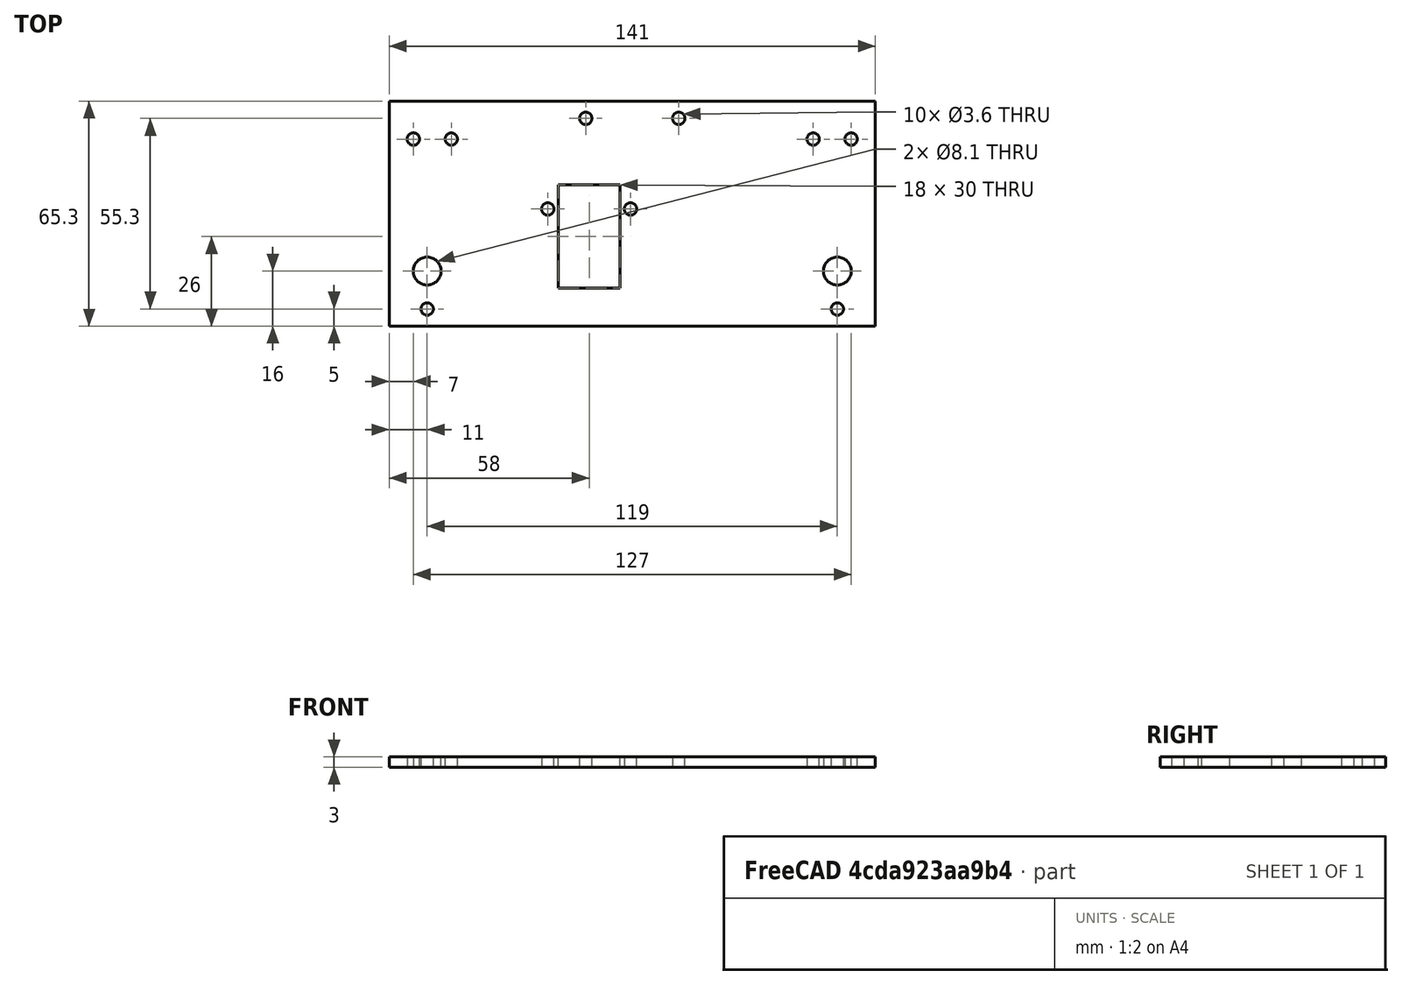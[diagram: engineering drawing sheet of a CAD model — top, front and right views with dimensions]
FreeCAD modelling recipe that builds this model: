
FCSTD DOCUMENT  (FreeCAD 0.16R6706 (Git))
Label: Plate Y Direita
License: All rights reserved
LicenseURL: http://en.wikipedia.org/wiki/All_rights_reserved
objects: Path::FeaturePython×16, Sketcher::SketchObject×1, PartDesign::Pad×1, Path::FeatureCompoundPython×1
note: 3 computed .brp shape members not serialized (recipe doc carries the construction recipe); baked Part::Feature solids carry a one-line shape summary decoded from their .brp

FEATURE [Sketcher::SketchObject] Sketch
  sketch-geometry (28):
    g0: LineSegment StartX=-141 StartY=65.3 StartZ=0 EndX=0 EndY=65.3 EndZ=0
    g1: LineSegment StartX=0 StartY=65.3 StartZ=0 EndX=0 EndY=0 EndZ=0
    g2: LineSegment StartX=0 StartY=0 StartZ=0 EndX=-141 EndY=0 EndZ=0
    g3: LineSegment StartX=-141 StartY=0 StartZ=0 EndX=-141 EndY=65.3 EndZ=0
    g4: Circle CenterX=-130 CenterY=16 CenterZ=0 NormalX=0 NormalY=0 NormalZ=1 Radius=4.05
    g5: Circle CenterX=-11 CenterY=16 CenterZ=0 NormalX=0 NormalY=0 NormalZ=1 Radius=4.05
    g6: LineSegment [constr] StartX=-130 StartY=16 StartZ=0 EndX=-11 EndY=16 EndZ=0
    g7: LineSegment [constr] StartX=-134 StartY=54.3 StartZ=0 EndX=-123 EndY=54.3 EndZ=0
    g8: Circle CenterX=-134 CenterY=54.3 CenterZ=0 NormalX=0 NormalY=0 NormalZ=1 Radius=1.8
    g9: Circle CenterX=-123 CenterY=54.3 CenterZ=0 NormalX=0 NormalY=0 NormalZ=1 Radius=1.8
    g10: LineSegment [constr] StartX=-18 StartY=54.3 StartZ=0 EndX=-7 EndY=54.3 EndZ=0
    g11: Circle CenterX=-18 CenterY=54.3 CenterZ=0 NormalX=0 NormalY=0 NormalZ=1 Radius=1.8
    g12: Circle CenterX=-7 CenterY=54.3 CenterZ=0 NormalX=0 NormalY=0 NormalZ=1 Radius=1.8
    g13: LineSegment StartX=-92 StartY=41 StartZ=0 EndX=-74 EndY=41 EndZ=0
    g14: LineSegment StartX=-74 StartY=41 StartZ=0 EndX=-74 EndY=11 EndZ=0
    g15: LineSegment StartX=-74 StartY=11 StartZ=0 EndX=-92 EndY=11 EndZ=0
    g16: LineSegment StartX=-92 StartY=11 StartZ=0 EndX=-92 EndY=41 EndZ=0
    g17: LineSegment [constr] StartX=-84 StartY=60.3 StartZ=0 EndX=-57 EndY=60.3 EndZ=0
    g18: LineSegment [constr] StartX=-70.5 StartY=60.3 StartZ=0 EndX=-70.5 EndY=65.3 EndZ=0
    g19: Circle CenterX=-84 CenterY=60.3 CenterZ=0 NormalX=0 NormalY=0 NormalZ=1 Radius=1.8
    g20: Circle CenterX=-57 CenterY=60.3 CenterZ=0 NormalX=0 NormalY=0 NormalZ=1 Radius=1.8
    g21: LineSegment [constr] StartX=-95 StartY=34 StartZ=0 EndX=-71 EndY=34 EndZ=0
    g22: Circle CenterX=-95 CenterY=34 CenterZ=0 NormalX=0 NormalY=0 NormalZ=1 Radius=1.8
    g23: Circle CenterX=-71 CenterY=34 CenterZ=0 NormalX=0 NormalY=0 NormalZ=1 Radius=1.8
    g24: LineSegment [constr] StartX=-130 StartY=5 StartZ=0 EndX=-11 EndY=5 EndZ=0
    g25: LineSegment [constr] StartX=-130 StartY=16 StartZ=0 EndX=-130 EndY=5 EndZ=0
    g26: Circle CenterX=-130 CenterY=5 CenterZ=0 NormalX=0 NormalY=0 NormalZ=1 Radius=1.8
    g27: Circle CenterX=-11 CenterY=5 CenterZ=0 NormalX=0 NormalY=0 NormalZ=1 Radius=1.8
  constraints (76):
    c: Coincident(g0,g1)
    c: Coincident(g1,g2)
    c: Coincident(g2,g3)
    c: Coincident(g3,g0)
    c: Horizontal(g0)
    c: Horizontal(g2)
    c: Vertical(g1)
    c: Vertical(g3)
    c: Coincident(g1,g-1)
    c: Radius(g4) = 4.05
    c: Equal(g4,g5) = 4.3
    c: Horizontal(g6)
    c: Coincident(g4,g6)
    c: Coincident(g5,g6)
    c: DistanceX(g2,g4) = 11
    c: DistanceX(g5,g-1) = 11
    c: DistanceX(g6,g6) = 119
    c: DistanceY(g2,g4) = 16
    c: DistanceY(g4,g0) = 49.3
    c: DistanceY(g2,g0) = 65.3
    c: Horizontal(g7)
    c: DistanceX(g7,g7) = 11
    c: Radius(g8) = 1.8
    c: Equal(g8,g9) = 1.8
    c: Coincident(g7,g9)
    c: Coincident(g7,g8)
    c: Horizontal(g10)
    c: Equal(g7,g10) = 10
    c: Equal(g8,g11) = 1.8
    c: Equal(g11,g12) = 1.8
    c: Coincident(g10,g12)
    c: Coincident(g10,g11)
    c: DistanceY(g7,g0) = 11
    c: PointOnObject(g10,g7)
    c: DistanceX(g0,g7) = 7
    c: DistanceX(g10,g0) = 7
    c: Coincident(g13,g14)
    c: Coincident(g14,g15)
    c: Coincident(g15,g16)
    c: Coincident(g16,g13)
    c: Horizontal(g13)
    c: Horizontal(g15)
    c: Vertical(g14)
    c: Vertical(g16)
    c: DistanceX(g15,g15) = 18
    c: DistanceY(g16,g16) = 30
    c: Horizontal(g17)
    c: DistanceX(g17,g17) = 27
    c: Vertical(g18)
    c: DistanceY(g18,g18) = 5
    c: Equal(g8,g19) = 1.8
    c: Equal(g8,g20) = 1.8
    c: Coincident(g17,g20)
    c: Coincident(g19,g17)
    c: Symmetric(g0,g0,g18)
    c: Symmetric(g17,g17,g18)
    c: DistanceY(g4,g13) = 25
    c: Horizontal(g21)
    c: DistanceX(g21,g21) = 24
    c: Equal(g8,g22) = 1.8
    c: Equal(g8,g23) = 1.8
    c: Coincident(g23,g21)
    c: Coincident(g21,g22)
    c: DistanceX(g21,g13) = 3
    c: DistanceY(g21,g13) = 7
    c: DistanceX(g4,g13) = 38
    c: Horizontal(g24)
    c: Equal(g6,g24) = 119
    c: Vertical(g25)
    c: Coincident(g25,g4)
    c: DistanceY(g25,g25) = 11
    c: Coincident(g24,g25)
    c: Equal(g8,g26) = 1.8
    c: Equal(g8,g27) = 1.8
    c: Coincident(g24,g27)
    c: Coincident(g24,g26)
FEATURE [PartDesign::Pad] Pad
  Length = 3
  Length2 = 100
  Sketch = -> Sketch
  Type = 0
FEATURE [Path::FeaturePython] Machine  label="Machine_"  # Path/CAM operation (typed FeaturePython)
  MachineUnits = 0
  X = 0
  X_Max = 0
  X_Min = 0
  Y = 0
  Y_Max = 0
  Y_Min = 0
  Z = 0
  Z_Max = 0
  Z_Min = 0
FEATURE [Path::FeaturePython] Tool  label="Tool1"  # Path/CAM operation (typed FeaturePython)
  SpindleDir = 0
  SpindleSpeed = 0
  ToolNumber = 1
FEATURE [Path::FeaturePython] Profile  label="Berço"  # Path/CAM operation (typed FeaturePython)
  Active = true
  Base = -> Pad
  ClearanceHeight = 3
  Direction = 1
  Edge1 = -> Pad [Edge48]
  EndPoint = (0,0,0)
  ExtendAtEnd = 0
  ExtendAtStart = 0
  FinalDepth = -5.1
  HorizFeed = 127
  LeadInLineLen = 0
  LeadOutLineLen = 0
  OffsetExtra = 0
  PathClosed = true
  RetractHeight = 0
  RollRadius = 0
  SegLen = 0.5
  Side = 1
  StartDepth = 0
  StartPoint = (0,0,0)
  StepDown = 2
  ToolNumber = 1
  UseEndPoint = false
  UsePlacements = false
  UseStartDepth = true
  UseStartPoint = false
  VertFeed = 127
FEATURE [Path::FeaturePython] Profile001  label="Berço001"  # Path/CAM operation (typed FeaturePython)
  Active = true
  Base = -> Pad
  ClearanceHeight = 3
  Direction = 1
  Edge1 = -> Pad [Edge45]
  EndPoint = (0,0,0)
  ExtendAtEnd = 0
  ExtendAtStart = 0
  FinalDepth = -5.1
  HorizFeed = 127
  LeadInLineLen = 0
  LeadOutLineLen = 0
  OffsetExtra = 0
  PathClosed = true
  RetractHeight = 0
  RollRadius = 0
  SegLen = 0.5
  Side = 1
  StartDepth = 0
  StartPoint = (0,0,0)
  StepDown = 2
  ToolNumber = 1
  UseEndPoint = false
  UsePlacements = false
  UseStartDepth = true
  UseStartPoint = false
  VertFeed = 127
FEATURE [Path::FeaturePython] Profile002  label="Berço002"  # Path/CAM operation (typed FeaturePython)
  Active = true
  Base = -> Pad
  ClearanceHeight = 3
  Direction = 1
  Edge1 = -> Pad [Edge57]
  EndPoint = (0,0,0)
  ExtendAtEnd = 0
  ExtendAtStart = 0
  FinalDepth = -5.1
  HorizFeed = 127
  LeadInLineLen = 0
  LeadOutLineLen = 0
  OffsetExtra = 0
  PathClosed = true
  RetractHeight = 0
  RollRadius = 0
  SegLen = 0.5
  Side = 1
  StartDepth = 0
  StartPoint = (0,0,0)
  StepDown = 2
  ToolNumber = 1
  UseEndPoint = false
  UsePlacements = false
  UseStartDepth = true
  UseStartPoint = false
  VertFeed = 127
FEATURE [Path::FeaturePython] Profile003  label="Berço003"  # Path/CAM operation (typed FeaturePython)
  Active = true
  Base = -> Pad
  ClearanceHeight = 3
  Direction = 1
  Edge1 = -> Pad [Edge54]
  EndPoint = (0,0,0)
  ExtendAtEnd = 0
  ExtendAtStart = 0
  FinalDepth = -5.1
  HorizFeed = 127
  LeadInLineLen = 0
  LeadOutLineLen = 0
  OffsetExtra = 0
  PathClosed = true
  RetractHeight = 0
  RollRadius = 0
  SegLen = 0.5
  Side = 1
  StartDepth = 0
  StartPoint = (0,0,0)
  StepDown = 2
  ToolNumber = 1
  UseEndPoint = false
  UsePlacements = false
  UseStartDepth = true
  UseStartPoint = false
  VertFeed = 127
FEATURE [Path::FeaturePython] Profile004  label="Suporte Correia"  # Path/CAM operation (typed FeaturePython)
  Active = true
  Base = -> Pad
  ClearanceHeight = 3
  Direction = 1
  Edge1 = -> Pad [Edge42]
  EndPoint = (0,0,0)
  ExtendAtEnd = 0
  ExtendAtStart = 0
  FinalDepth = -5.1
  HorizFeed = 127
  LeadInLineLen = 0
  LeadOutLineLen = 0
  OffsetExtra = 0
  PathClosed = true
  RetractHeight = 0
  RollRadius = 0
  SegLen = 0.5
  Side = 1
  StartDepth = 0
  StartPoint = (0,0,0)
  StepDown = 2
  ToolNumber = 1
  UseEndPoint = false
  UsePlacements = false
  UseStartDepth = true
  UseStartPoint = false
  VertFeed = 127
FEATURE [Path::FeaturePython] Profile005  label="Suporte Correia001"  # Path/CAM operation (typed FeaturePython)
  Active = true
  Base = -> Pad
  ClearanceHeight = 3
  Direction = 1
  Edge1 = -> Pad [Edge39]
  EndPoint = (0,0,0)
  ExtendAtEnd = 0
  ExtendAtStart = 0
  FinalDepth = -5.1
  HorizFeed = 127
  LeadInLineLen = 0
  LeadOutLineLen = 0
  OffsetExtra = 0
  PathClosed = true
  RetractHeight = 0
  RollRadius = 0
  SegLen = 0.5
  Side = 1
  StartDepth = 0
  StartPoint = (0,0,0)
  StepDown = 2
  ToolNumber = 1
  UseEndPoint = false
  UsePlacements = false
  UseStartDepth = true
  UseStartPoint = false
  VertFeed = 127
FEATURE [Path::FeaturePython] Profile006  label="Eixo"  # Path/CAM operation (typed FeaturePython)
  Active = true
  Base = -> Pad
  ClearanceHeight = 3
  Direction = 1
  Edge1 = -> Pad [Edge27]
  EndPoint = (0,0,0)
  ExtendAtEnd = 0
  ExtendAtStart = 0
  FinalDepth = -5.1
  HorizFeed = 127
  LeadInLineLen = 0
  LeadOutLineLen = 0
  OffsetExtra = 0
  PathClosed = true
  RetractHeight = 0
  RollRadius = 0
  SegLen = 0.5
  Side = 1
  StartDepth = 0
  StartPoint = (0,0,0)
  StepDown = 2
  ToolNumber = 1
  UseEndPoint = false
  UsePlacements = false
  UseStartDepth = true
  UseStartPoint = false
  VertFeed = 127
FEATURE [Path::FeaturePython] Profile007  label="Eixo001"  # Path/CAM operation (typed FeaturePython)
  Active = true
  Base = -> Pad
  ClearanceHeight = 3
  Direction = 1
  Edge1 = -> Pad [Edge30]
  EndPoint = (0,0,0)
  ExtendAtEnd = 0
  ExtendAtStart = 0
  FinalDepth = -5.1
  HorizFeed = 127
  LeadInLineLen = 0
  LeadOutLineLen = 0
  OffsetExtra = 0
  PathClosed = true
  RetractHeight = 0
  RollRadius = 0
  SegLen = 0.5
  Side = 1
  StartDepth = 0
  StartPoint = (0,0,0)
  StepDown = 2
  ToolNumber = 1
  UseEndPoint = false
  UsePlacements = false
  UseStartDepth = true
  UseStartPoint = false
  VertFeed = 127
FEATURE [Path::FeaturePython] Profile008  label="apoio polia"  # Path/CAM operation (typed FeaturePython)
  Active = true
  Base = -> Pad
  ClearanceHeight = 3
  Direction = 1
  Edge1 = -> Pad [Edge36]
  EndPoint = (0,0,0)
  ExtendAtEnd = 0
  ExtendAtStart = 0
  FinalDepth = -5.1
  HorizFeed = 127
  LeadInLineLen = 0
  LeadOutLineLen = 0
  OffsetExtra = 0
  PathClosed = true
  RetractHeight = 0
  RollRadius = 0
  SegLen = 0.5
  Side = 1
  StartDepth = 0
  StartPoint = (0,0,0)
  StepDown = 2
  ToolNumber = 1
  UseEndPoint = false
  UsePlacements = false
  UseStartDepth = true
  UseStartPoint = false
  VertFeed = 127
FEATURE [Path::FeaturePython] Profile009  label="apoio polia001"  # Path/CAM operation (typed FeaturePython)
  Active = true
  Base = -> Pad
  ClearanceHeight = 3
  Direction = 1
  Edge1 = -> Pad [Edge33]
  EndPoint = (0,0,0)
  ExtendAtEnd = 0
  ExtendAtStart = 0
  FinalDepth = -5.1
  HorizFeed = 127
  LeadInLineLen = 0
  LeadOutLineLen = 0
  OffsetExtra = 0
  PathClosed = true
  RetractHeight = 0
  RollRadius = 0
  SegLen = 0.5
  Side = 1
  StartDepth = 0
  StartPoint = (0,0,0)
  StepDown = 2
  ToolNumber = 1
  UseEndPoint = false
  UsePlacements = false
  UseStartDepth = true
  UseStartPoint = false
  VertFeed = 127
FEATURE [Path::FeaturePython] Profile010  label="Janela"  # Path/CAM operation (typed FeaturePython)
  Active = true
  Base = -> Pad
  ClearanceHeight = 3
  Direction = 1
  Edge1 = -> Pad [Edge24]
  Edge2 = -> Pad [Edge22]
  EndPoint = (0,0,0)
  ExtendAtEnd = 0
  ExtendAtStart = 0
  FinalDepth = -5.1
  HorizFeed = 127
  LeadInLineLen = 0
  LeadOutLineLen = 0
  OffsetExtra = 0
  PathClosed = true
  RetractHeight = 0
  RollRadius = 0
  SegLen = 0.5
  Side = 1
  StartDepth = 0
  StartPoint = (0,0,0)
  StepDown = 2
  ToolNumber = 1
  UseEndPoint = false
  UsePlacements = false
  UseStartDepth = true
  UseStartPoint = false
  VertFeed = 127
FEATURE [Path::FeaturePython] Profile011  label="Fixacao"  # Path/CAM operation (typed FeaturePython)
  Active = true
  Base = -> Pad
  ClearanceHeight = 3
  Direction = 1
  Edge1 = -> Pad [Edge51]
  EndPoint = (0,0,0)
  ExtendAtEnd = 0
  ExtendAtStart = 0
  FinalDepth = -5.1
  HorizFeed = 127
  LeadInLineLen = 0
  LeadOutLineLen = 0
  OffsetExtra = 0
  PathClosed = true
  RetractHeight = 0
  RollRadius = 0
  SegLen = 0.5
  Side = 1
  StartDepth = 0
  StartPoint = (0,0,0)
  StepDown = 2
  ToolNumber = 1
  UseEndPoint = false
  UsePlacements = false
  UseStartDepth = true
  UseStartPoint = false
  VertFeed = 127
FEATURE [Path::FeaturePython] Profile012  label="Fixacao001"  # Path/CAM operation (typed FeaturePython)
  Active = true
  Base = -> Pad
  ClearanceHeight = 3
  Direction = 1
  Edge1 = -> Pad [Edge60]
  EndPoint = (0,0,0)
  ExtendAtEnd = 0
  ExtendAtStart = 0
  FinalDepth = -5.1
  HorizFeed = 127
  LeadInLineLen = 0
  LeadOutLineLen = 0
  OffsetExtra = 0
  PathClosed = true
  RetractHeight = 0
  RollRadius = 0
  SegLen = 0.5
  Side = 1
  StartDepth = 0
  StartPoint = (0,0,0)
  StepDown = 2
  ToolNumber = 1
  UseEndPoint = false
  UsePlacements = false
  UseStartDepth = true
  UseStartPoint = false
  VertFeed = 127
FEATURE [Path::FeaturePython] Profile013  label="Externo"  # Path/CAM operation (typed FeaturePython)
  Active = true
  Base = -> Pad
  ClearanceHeight = 3
  Direction = 0
  EndPoint = (0,0,0)
  ExtendAtEnd = 0
  ExtendAtStart = 0
  Face1 = -> Pad [Face22]
  FinalDepth = -5.1
  HorizFeed = 127
  LeadInLineLen = 0
  LeadOutLineLen = 0
  OffsetExtra = 0
  PathClosed = true
  RetractHeight = 0
  RollRadius = 0
  SegLen = 0.5
  Side = 0
  StartDepth = 0
  StartPoint = (0,0,0)
  StepDown = 2
  ToolNumber = 1
  UseEndPoint = false
  UsePlacements = false
  UseStartDepth = true
  UseStartPoint = false
  VertFeed = 127
FEATURE [Path::FeatureCompoundPython] Project  # Path/CAM operation (typed FeaturePython)
  Group = -> [Machine,Tool,Profile,Profile001,Profile002,Profile003,Profile004,Profile005,Profile006,Profile007,Profile008,Profile009,Profile010,Profile011,Profile012,Profile013]
  UsePlacements = false
